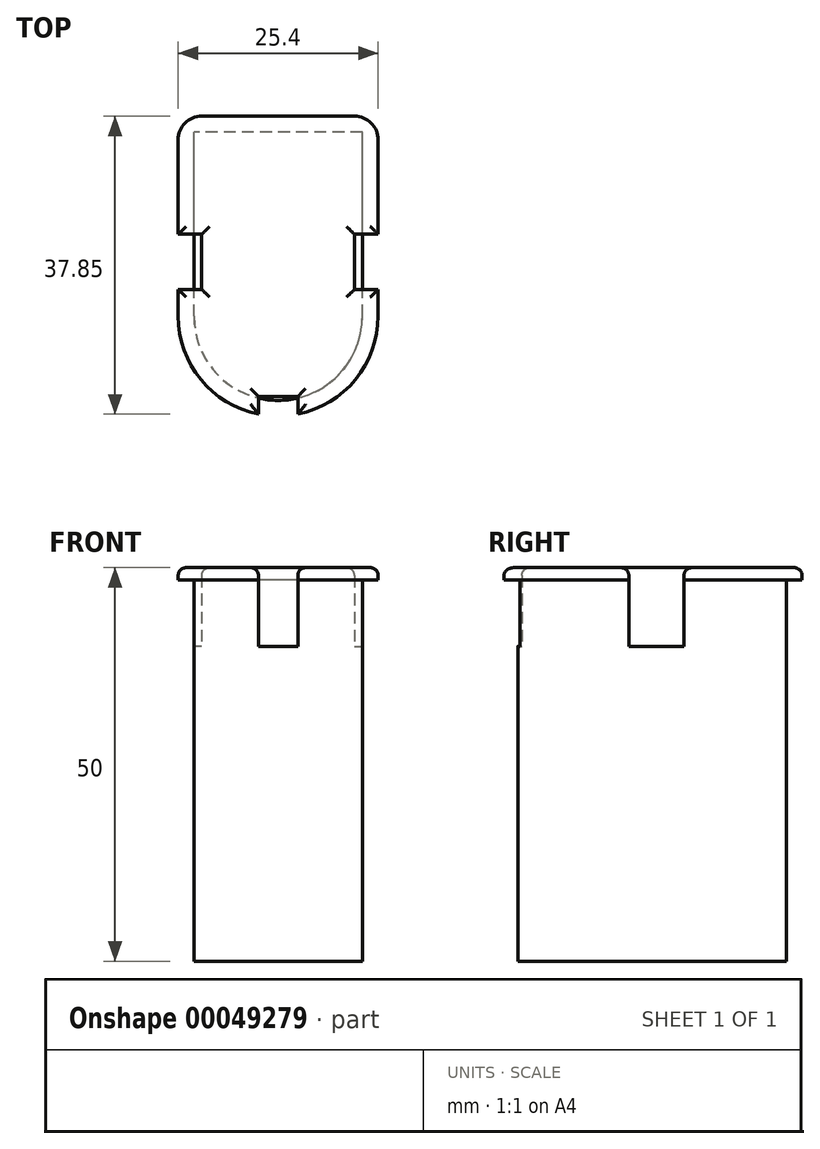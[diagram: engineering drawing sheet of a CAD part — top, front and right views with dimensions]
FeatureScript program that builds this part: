
annotation { "Feature Type Name" : "Feature", "Feature Type Description" : "" }
export const myFeature = defineFeature(function(context is Context, id is Id, definition is map)
    precondition{}
    {
        {
            var Q0;
            Q0=qCreatedBy(makeId("Top.planeOp"),FACE);
            var sketch = newSketch(context, id + "F0", { "sketchPlane" : qUnion([Q0])});
            skLineSegment(sketch, "E0.rect.bottom", {"start": v(0, -19.05) * mm, "end": v(0, -19.05) * mm});
            skLineSegment(sketch, "E0.rect.top", {"start": v(9.7, 19.05) * mm, "end": v(-9.7, 19.05) * mm});
            skLineSegment(sketch, "E0.rect.left", {"start": v(12.7, -6.35) * mm, "end": v(12.7, 16.05) * mm});
            skLineSegment(sketch, "E0.rect.right", {"start": v(-12.7, -6.35) * mm, "end": v(-12.7, 16.05) * mm});
            skPoint(sketch, "E0.rect.middle", {"position": v(0, 0) * mm});
            skPoint(sketch, "E1.visualSharp", {"position": v(-12.7, -19.05) * mm});
            skArc(sketch, "E1.filletArc", {"start": v(-12.7, -6.35) * mm, "mid": v(-8.98, -15.33) * mm, "end": v(0, -19.05) * mm});
            skPoint(sketch, "E2.visualSharp", {"position": v(12.7, -19.05) * mm});
            skArc(sketch, "E2.filletArc", {"start": v(0, -19.05) * mm, "mid": v(8.98, -15.33) * mm, "end": v(12.7, -6.35) * mm});
            skPoint(sketch, "E3.visualSharp", {"position": v(-12.7, 19.05) * mm});
            skArc(sketch, "E3.filletArc", {"start": v(-9.7, 19.05) * mm, "mid": v(-11.82, 18.17) * mm, "end": v(-12.7, 16.05) * mm});
            skPoint(sketch, "E4.visualSharp", {"position": v(12.7, 19.05) * mm});
            skArc(sketch, "E4.filletArc", {"start": v(12.7, 16.05) * mm, "mid": v(11.82, 18.17) * mm, "end": v(9.7, 19.05) * mm});
            skLineSegment(sketch, "E5.rect.bottom", {"start": v(2.5, -21.55) * mm, "end": v(-2.5, -21.55) * mm});
            skLineSegment(sketch, "E5.rect.top", {"start": v(2.5, -16.55) * mm, "end": v(-2.5, -16.55) * mm});
            skLineSegment(sketch, "E5.rect.left", {"start": v(2.5, -21.55) * mm, "end": v(2.5, -16.55) * mm});
            skLineSegment(sketch, "E5.rect.right", {"start": v(-2.5, -21.55) * mm, "end": v(-2.5, -16.55) * mm});
            skPoint(sketch, "E5.rect.middle", {"position": v(0, -19.05) * mm});
            skLineSegment(sketch, "E6", {"start": v(0, 27.45) * mm, "end": v(0, -34.54) * mm, "construction": true});
            skPoint(sketch, "E6.endSnap0", {"position": v(0, -21.55) * mm});
            skLineSegment(sketch, "E7.rect.bottom", {"start": v(-9.7, -2.95) * mm, "end": v(-15.7, -2.95) * mm});
            skLineSegment(sketch, "E7.rect.top", {"start": v(-9.7, 4.05) * mm, "end": v(-15.7, 4.05) * mm});
            skLineSegment(sketch, "E7.rect.left", {"start": v(-9.7, -2.95) * mm, "end": v(-9.7, 4.05) * mm});
            skLineSegment(sketch, "E7.rect.right", {"start": v(-15.7, -2.95) * mm, "end": v(-15.7, 4.05) * mm});
            skPoint(sketch, "E7.rect.middle", {"position": v(-12.7, 0.55) * mm});
            skLineSegment(sketch, "E8.MirrorCS", {"start": v(9.7, -2.95) * mm, "end": v(15.7, -2.95) * mm});
            skLineSegment(sketch, "E9.MirrorCS", {"start": v(15.7, -2.95) * mm, "end": v(15.7, 4.05) * mm});
            skLineSegment(sketch, "E10.MirrorCS", {"start": v(9.7, 4.05) * mm, "end": v(15.7, 4.05) * mm});
            skLineSegment(sketch, "E11.MirrorCS", {"start": v(9.7, -2.95) * mm, "end": v(9.7, 4.05) * mm});
            skSolve(sketch);
        }
        {
            var Q0;
            Q0=makeQuery(id+"F0.imprint","IMPRINT",FACE,{"disambiguationData":[TD([[makeQuery(id+"F0.imprint","IMPRINT",EDGE,{"derivedFrom":sQuery(id+"F0.wireOp",EDGE,"E0.rect.top")}),1.0]])]});
            extrude(context, id + "F1", {"entities" : qUnion([Q0]), "depth" : 10 * mm});
        }
        {
            var Q0;
            Q0=makeQuery(id+"F0.imprint","IMPRINT",FACE,{"disambiguationData":[TD([[makeQuery(id+"F0.imprint","IMPRINT",EDGE,{"derivedFrom":sQuery(id+"F0.wireOp",EDGE,"E0.rect.top")}),1.0]])]});
            var Q1;
            {var subQ5=sQuery(id+"F0.wireOp",EDGE,"E11.MirrorCS");Q1=makeQuery(id+"F0.imprint","IMPRINT",FACE,{"disambiguationData":[TD([[makeQuery(id+"F0.imprint","IMPRINT",EDGE,{"derivedFrom":subQ5}),-1.0]])]});}
            var Q2;
            {var subQ1=sQuery(id+"F0.wireOp",EDGE,"E5.rect.top");Q2=makeQuery(id+"F0.imprint","IMPRINT",FACE,{"disambiguationData":[TD([[makeQuery(id+"F0.imprint","IMPRINT",EDGE,{"derivedFrom":subQ1}),1.0]])]});}
            var Q3;
            {var subQ5=sQuery(id+"F0.wireOp",EDGE,"E7.rect.left");Q3=makeQuery(id+"F0.imprint","IMPRINT",FACE,{"disambiguationData":[TD([[makeQuery(id+"F0.imprint","IMPRINT",EDGE,{"derivedFrom":subQ5}),1.0]])]});}
            extrude(context, id + "F2", {"entities" : qUnion([Q0, Q1, Q2, Q3]), "operationType" : NewBodyOperationType.ADD, "oppositeDirection" : true, "depth" : 40 * mm});
        }
        {
            var Q0;
            Q0=makeQuery(id+"F2.opExtrude","CAP_FACE",FACE,{"disambiguationData":[OSD([sQuery(id+"F0.wireOp",EDGE,"E0.rect.top"),sQuery(id+"F0.wireOp",EDGE,"E0.rect.left"),sQuery(id+"F0.wireOp",EDGE,"E0.rect.right"),sQuery(id+"F0.wireOp",EDGE,"E1.filletArc"),sQuery(id+"F0.wireOp",EDGE,"E2.filletArc"),sQuery(id+"F0.wireOp",EDGE,"E3.filletArc"),sQuery(id+"F0.wireOp",EDGE,"E4.filletArc")])],"isStart":false});
            var sketch = newSketch(context, id + "F3", { "sketchPlane" : qUnion([Q0])});
            skArc(sketch, "E12.0", {"start": v(-12.7, 6.35) * mm, "mid": v(0, 19.05) * mm, "end": v(12.7, 6.35) * mm});
            skLineSegment(sketch, "E12.1", {"start": v(12.7, 6.35) * mm, "end": v(12.7, -16.05) * mm});
            skArc(sketch, "E12.2", {"start": v(12.7, -16.05) * mm, "mid": v(11.82, -18.17) * mm, "end": v(9.7, -19.05) * mm});
            skLineSegment(sketch, "E12.3", {"start": v(9.7, -19.05) * mm, "end": v(-9.7, -19.05) * mm});
            skArc(sketch, "E12.4", {"start": v(-9.7, -19.05) * mm, "mid": v(-11.82, -18.17) * mm, "end": v(-12.7, -16.05) * mm});
            skLineSegment(sketch, "E12.5", {"start": v(-12.7, 6.35) * mm, "end": v(-12.7, -16.05) * mm});
            skArc(sketch, "E13.0", {"start": v(-10.7, 6.35) * mm, "mid": v(0, 17.05) * mm, "end": v(10.7, 6.35) * mm});
            skLineSegment(sketch, "E13.1", {"start": v(-10.7, 6.35) * mm, "end": v(-10.7, -17.05) * mm});
            skLineSegment(sketch, "E13.2", {"start": v(10.7, -17.05) * mm, "end": v(-10.7, -17.05) * mm});
            skLineSegment(sketch, "E13.3", {"start": v(10.7, 6.35) * mm, "end": v(10.7, -17.05) * mm});
            skSolve(sketch);
        }
        {
            var Q0;
            Q0=makeQuery(id+"F3.imprint","IMPRINT",FACE,{"disambiguationData":[TD([[makeQuery(id+"F3.imprint","IMPRINT",EDGE,{"derivedFrom":sQuery(id+"F3.wireOp",EDGE,"E13.0")}),-1.0]])]});
            extrude(context, id + "F4", {"entities" : qUnion([Q0]), "operationType" : NewBodyOperationType.REMOVE, "oppositeDirection" : true, "depth" : 48.43 * mm});
        }
        {
            var Q0;
            Q0=makeQuery(id+"F1.opExtrude","CAP_FACE",FACE,{"disambiguationData":[OSD([sQuery(id+"F0.wireOp",EDGE,"E0.rect.top"),sQuery(id+"F0.wireOp",EDGE,"E0.rect.left"),sQuery(id+"F0.wireOp",EDGE,"E0.rect.right"),sQuery(id+"F0.wireOp",EDGE,"E1.filletArc"),sQuery(id+"F0.wireOp",EDGE,"E2.filletArc"),sQuery(id+"F0.wireOp",EDGE,"E3.filletArc"),sQuery(id+"F0.wireOp",EDGE,"E4.filletArc"),sQuery(id+"F0.wireOp",EDGE,"E5.rect.top"),sQuery(id+"F0.wireOp",EDGE,"E5.rect.left"),sQuery(id+"F0.wireOp",EDGE,"E5.rect.right"),sQuery(id+"F0.wireOp",EDGE,"E7.rect.bottom"),sQuery(id+"F0.wireOp",EDGE,"E7.rect.top"),sQuery(id+"F0.wireOp",EDGE,"E7.rect.left"),sQuery(id+"F0.wireOp",EDGE,"E8.MirrorCS"),sQuery(id+"F0.wireOp",EDGE,"E10.MirrorCS"),sQuery(id+"F0.wireOp",EDGE,"E11.MirrorCS")])],"isStart":false});
            fillet(context, id + "F5", {"entities" : qUnion([Q0]), "radius" : 1 * mm, "tangentPropagation" : true, "allowEdgeOverflow" : false});
        }
    });
